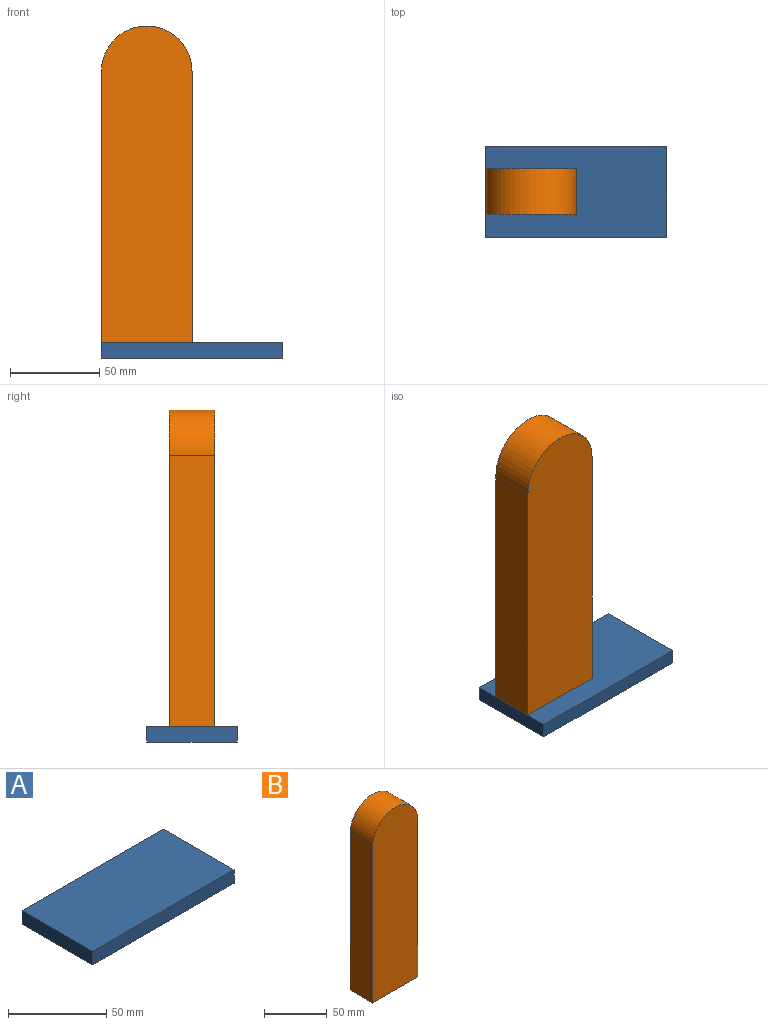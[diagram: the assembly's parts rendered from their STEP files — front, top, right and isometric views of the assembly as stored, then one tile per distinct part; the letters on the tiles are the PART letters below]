
ASSEMBLY  parts=2 mates=1
PART A: 6 faces, bbox 101.6x50.8x8.5 mm
  f0: plane 50.8x8.47mm, normal (1,0,0), area 430.1mm2, adj f1,f3,f4,f5
  f1: plane 101.6x8.47mm, normal (0,1,0), area 860.2mm2, adj f0,f2,f4,f5
  f2: plane 50.8x8.47mm, normal (-1,0,0), area 430.1mm2, adj f1,f3,f4,f5
  f3: plane 101.6x8.47mm, normal (0,-1,0), area 860.2mm2, adj f0,f2,f4,f5
  f4: plane 101.6x50.8mm, normal (0,0,1), area 5161.3mm2, adj f0,f1,f2,f3
  f5: plane 101.6x50.8mm, normal (0,0,-1), area 5161.3mm2, adj f0,f1,f2,f3
PART B: 6 faces, bbox 50.8x25.4x177.8 mm
  f0: plane 152.4x25.4mm, normal (-1,0,0), area 3871mm2, adj f1,f3,f4,f5
  f1: plane 50.8x25.4mm, normal (0,0,-1), area 1290.3mm2, adj f0,f2,f4,f5
  f2: plane 152.4x25.4mm, normal (1,0,0), area 3871mm2, adj f1,f3,f4,f5
  f3: cylinder r=25.4mm len=50.8mm, axis (0,1,0), area 2026.8mm2, adj f0,f2,f4,f5
  f4: plane 177.8x50.8mm, normal (0,-1,0), area 8755.3mm2, adj f0,f1,f2,f3
  f5: plane 177.8x50.8mm, normal (0,1,0), area 8755.3mm2, adj f0,f1,f2,f3
PLACE A t=(50.8,0,0)mm
PLACE B t=(25.4,0,8.47)mm
MATE fastened B.f1 <-> A.f4  axis (0,0,-1) through (0,0,8.47)mm
